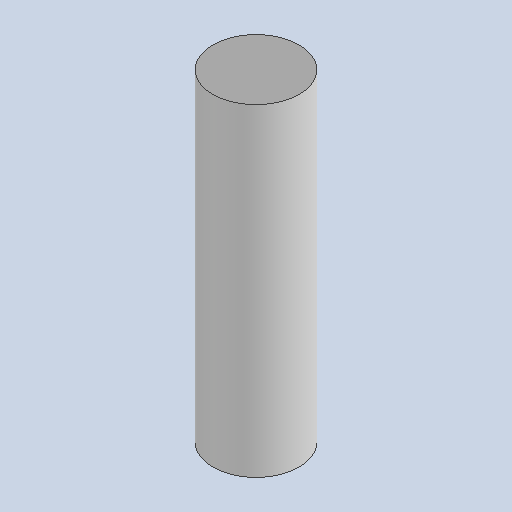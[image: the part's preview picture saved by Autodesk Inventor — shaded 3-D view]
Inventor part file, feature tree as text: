
AUTODESK INVENTOR PART (.ipt)
format: ipt  version: 2025 (Build 290162010, 162A)  size: 78,848 bytes
history: native  units: mm
features: extrude x1, sketch x1
ambient origin geometry x8: Origin, YZ Plane, XZ Plane, XY Plane, X Axis, Y Axis, Z Axis, Center Point
bodies: Solid1 (feature_tree)
feature tree (2):
  extrude  "Extrusion1"  Depth=45.0mm TaperAngle=0.0deg
  sketch  "Sketch1"  dims[d0=12.0mm d1=45.0mm d2=40.0mm d3=0.0mm d4=0.0mm]
